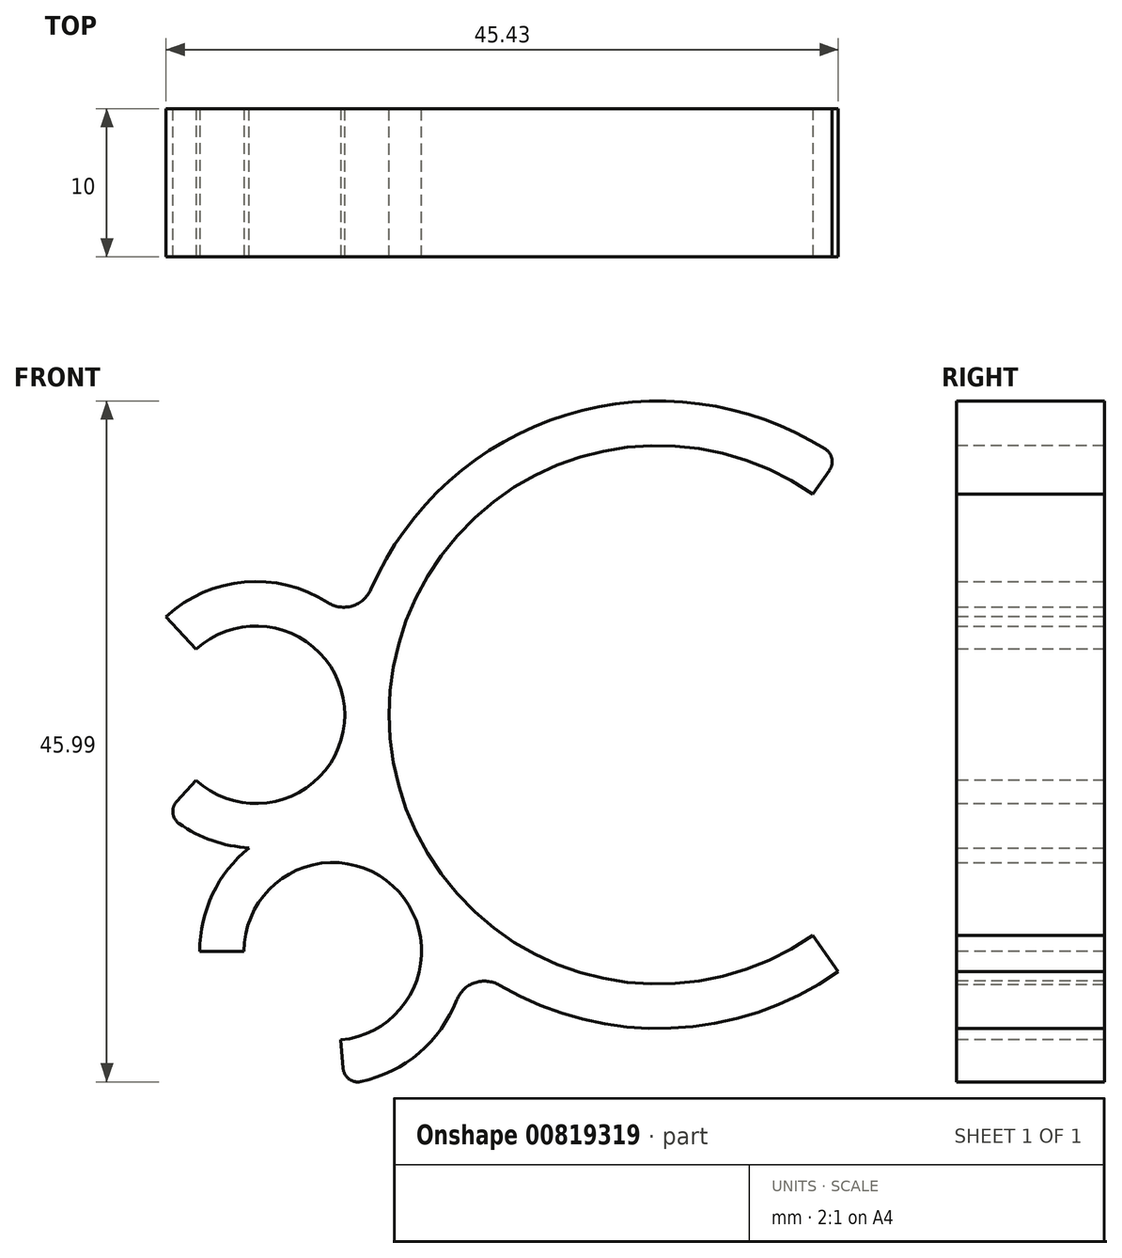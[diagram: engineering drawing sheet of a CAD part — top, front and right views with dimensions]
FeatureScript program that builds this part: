
annotation { "Feature Type Name" : "Feature", "Feature Type Description" : "" }
export const myFeature = defineFeature(function(context is Context, id is Id, definition is map)
    precondition{}
    {
        {
            var Q0;
            Q0=qCreatedBy(makeId("Front.planeOp"),FACE);
            var sketch = newSketch(context, id + "F0", { "sketchPlane" : qUnion([Q0])});
            skCircle(sketch, "E0", {"center": v(0, 0) * mm, "radius": 18.2 * mm});
            skCircle(sketch, "E1", {"center": v(0, 0) * mm, "radius": 21.2 * mm});
            skCircle(sketch, "E2", {"center": v(-27.2, 0) * mm, "radius": 6 * mm});
            skCircle(sketch, "E3", {"center": v(-27.2, 0) * mm, "radius": 9 * mm});
            skSolve(sketch);
        }
        {
            var Q0;
            Q0 = qSketchRegion(id + "F0", true);
            extrude(context, id + "F1", {"entities" : qUnion([Q0]), "endBound" : BoundingType.SYMMETRIC, "depth" : 10 * mm, "offsetDistance" : 25 * mm});
        }
        {
            var Q0;
            {var subQ0=sQuery(id+"F0.wireOp",EDGE,"E3");var subQ1=sQuery(id+"F0.wireOp",EDGE,"E1");Q0=makeQuery(id+"F1.opExtrude","SWEPT_EDGE",EDGE,{"disambiguationData":[OSD([subQ1,subQ0]),TDD([makeQuery(id+"F0.imprint","INTERSECT",VERTEX,{"disambiguationData":[OD(0.0)],"derivedFrom":[subQ1,subQ0]})])]});}
            var Q1;
            {var subQ0=sQuery(id+"F0.wireOp",EDGE,"E3");var subQ1=sQuery(id+"F0.wireOp",EDGE,"E1");Q1=makeQuery(id+"F1.opExtrude","SWEPT_EDGE",EDGE,{"disambiguationData":[OSD([subQ1,subQ0]),TDD([makeQuery(id+"F0.imprint","INTERSECT",VERTEX,{"disambiguationData":[OD(1.0)],"derivedFrom":[subQ1,subQ0]})])]});}
            fillet(context, id + "F2", {"entities" : qUnion([Q0, Q1]), "radius" : 2 * mm, "tangentPropagation" : true, "allowEdgeOverflow" : false});
        }
        {
            var Q0;
            Q0=makeQuery(id+"F1.opExtrude","SWEPT_BODY",BODY,{"disambiguationData":[OSD([sQuery(id+"F0.wireOp",EDGE,"E0"),sQuery(id+"F0.wireOp",EDGE,"E1"),sQuery(id+"F0.wireOp",EDGE,"E2"),sQuery(id+"F0.wireOp",EDGE,"E3")])]});
            var Q1;
            Q1=makeQuery(id+"F1.opExtrude","SWEPT_FACE",FACE,{"disambiguationData":[OSD([sQuery(id+"F0.wireOp",EDGE,"E0")])]});
            circularPattern(context, id + "F3", {"operationType" : NewBodyOperationType.ADD, "entities" : qUnion([Q0]), "axis" : qUnion([Q1]), "angle" : 36 * degree, "instanceCount" : 2, "equalSpace" : true});
        }
        {
            var Q0;
            Q0=makeQuery(id+"F1.opExtrude","CAP_FACE",FACE,{"disambiguationData":[OSD([sQuery(id+"F0.wireOp",EDGE,"E0"),sQuery(id+"F0.wireOp",EDGE,"E1"),sQuery(id+"F0.wireOp",EDGE,"E2"),sQuery(id+"F0.wireOp",EDGE,"E3")])],"isStart":false});
            var sketch = newSketch(context, id + "F4", { "sketchPlane" : qUnion([Q0])});
            skLineSegment(sketch, "E4", {"start": v(-31.25, 4.42) * mm, "end": v(-33.27, 6.64) * mm});
            skLineSegment(sketch, "E5", {"start": v(-31.25, -4.42) * mm, "end": v(-33.27, -6.64) * mm});
            skLineSegment(sketch, "E6", {"start": v(10.44, 14.9) * mm, "end": v(12.16, 17.36) * mm});
            skLineSegment(sketch, "E7", {"start": v(10.44, -14.9) * mm, "end": v(12.16, -17.36) * mm});
            skCircle(sketch, "E8.0", {"center": v(-27.2, 0) * mm, "radius": 6 * mm});
            skArc(sketch, "E9", {"start": v(-33.27, 6.64) * mm, "mid": v(-36.2, 0) * mm, "end": v(-33.27, -6.64) * mm});
            skArc(sketch, "E10", {"start": v(-31.25, 4.42) * mm, "mid": v(-33.2, 0) * mm, "end": v(-31.25, -4.42) * mm});
            skArc(sketch, "E11", {"start": v(10.44, 14.9) * mm, "mid": v(18.2, 0) * mm, "end": v(10.44, -14.9) * mm});
            skArc(sketch, "E12", {"start": v(12.16, 17.36) * mm, "mid": v(21.2, 0) * mm, "end": v(12.16, -17.36) * mm});
            skLineSegment(sketch, "E13", {"start": v(-28, -15.98) * mm, "end": v(-31, -15.98) * mm});
            skLineSegment(sketch, "E14", {"start": v(-21.48, -21.96) * mm, "end": v(-21.22, -24.95) * mm});
            skCircle(sketch, "E15.0", {"center": v(-22, -15.98) * mm, "radius": 6 * mm});
            skArc(sketch, "E16", {"start": v(-31, -15.98) * mm, "mid": v(-28.08, -22.62) * mm, "end": v(-21.22, -24.95) * mm});
            skArc(sketch, "E17", {"start": v(-28, -15.98) * mm, "mid": v(-26.05, -20.4) * mm, "end": v(-21.48, -21.96) * mm});
            skSolve(sketch);
        }
        {
            var Q0;
            {var subQ0=sQuery(id+"F4.wireOp",EDGE,"E4");Q0=makeQuery(id+"F4.imprint","IMPRINT",FACE,{"disambiguationData":[TD([[makeQuery(id+"F4.imprint","IMPRINT",EDGE,{"derivedFrom":subQ0}),1.0]])]});}
            var Q1;
            Q1=makeQuery(id+"F4.imprint","IMPRINT",FACE,{"disambiguationData":[TD([[makeQuery(id+"F4.imprint","IMPRINT",EDGE,{"derivedFrom":sQuery(id+"F4.wireOp",EDGE,"E6")}),-1.0]])]});
            var Q2;
            {var subQ0=sQuery(id+"F4.wireOp",EDGE,"E13");Q2=makeQuery(id+"F4.imprint","IMPRINT",FACE,{"disambiguationData":[TD([[makeQuery(id+"F4.imprint","IMPRINT",EDGE,{"derivedFrom":subQ0}),1.0]])]});}
            extrude(context, id + "F5", {"entities" : qUnion([Q0, Q1, Q2]), "operationType" : NewBodyOperationType.REMOVE, "endBound" : BoundingType.THROUGH_ALL, "oppositeDirection" : true, "depth" : 25 * mm, "offsetDistance" : 25 * mm});
        }
        {
            var Q0;
            Q0=makeQuery(id+"F5.boolean.opBoolean","COPY",EDGE,{"derivedFrom":makeQuery(id+"F5.opExtrude","SWEPT_EDGE",EDGE,{"disambiguationData":[OSD([sQuery(id+"F4.wireOp",EDGE,"E4"),sQuery(id+"F4.wireOp",EDGE,"E8.0")])]})});
            var Q1;
            Q1=makeQuery(id+"F5.boolean.opBoolean","COPY",EDGE,{"derivedFrom":makeQuery(id+"F5.opExtrude","SWEPT_EDGE",EDGE,{"disambiguationData":[OSD([sQuery(id+"F0.wireOp",EDGE,"E3"),sQuery(id+"F4.wireOp",EDGE,"E4"),sQuery(id+"F4.wireOp",EDGE,"E9")])]})});
            var Q2;
            Q2=makeQuery(id+"F5.boolean.opBoolean","COPY",EDGE,{"derivedFrom":makeQuery(id+"F5.opExtrude","SWEPT_EDGE",EDGE,{"disambiguationData":[OSD([sQuery(id+"F0.wireOp",EDGE,"E3"),sQuery(id+"F4.wireOp",EDGE,"E5"),sQuery(id+"F4.wireOp",EDGE,"E9")])]})});
            var Q3;
            Q3=makeQuery(id+"F5.boolean.opBoolean","COPY",EDGE,{"derivedFrom":makeQuery(id+"F5.opExtrude","SWEPT_EDGE",EDGE,{"disambiguationData":[OSD([sQuery(id+"F4.wireOp",EDGE,"E5"),sQuery(id+"F4.wireOp",EDGE,"E8.0")])]})});
            var Q4;
            Q4=makeQuery(id+"F5.boolean.opBoolean","COPY",EDGE,{"derivedFrom":makeQuery(id+"F5.opExtrude","SWEPT_EDGE",EDGE,{"disambiguationData":[OSD([sQuery(id+"F0.wireOp",EDGE,"E0"),sQuery(id+"F4.wireOp",EDGE,"E6"),sQuery(id+"F4.wireOp",EDGE,"E11")])]})});
            var Q5;
            Q5=makeQuery(id+"F5.boolean.opBoolean","COPY",EDGE,{"derivedFrom":makeQuery(id+"F5.opExtrude","SWEPT_EDGE",EDGE,{"disambiguationData":[OSD([sQuery(id+"F0.wireOp",EDGE,"E1"),sQuery(id+"F4.wireOp",EDGE,"E6"),sQuery(id+"F4.wireOp",EDGE,"E12")])]})});
            var Q6;
            Q6=makeQuery(id+"F5.boolean.opBoolean","COPY",EDGE,{"derivedFrom":makeQuery(id+"F5.opExtrude","SWEPT_EDGE",EDGE,{"disambiguationData":[OSD([sQuery(id+"F0.wireOp",EDGE,"E1"),sQuery(id+"F4.wireOp",EDGE,"E7"),sQuery(id+"F4.wireOp",EDGE,"E12")])]})});
            var Q7;
            Q7=makeQuery(id+"F5.boolean.opBoolean","COPY",EDGE,{"derivedFrom":makeQuery(id+"F5.opExtrude","SWEPT_EDGE",EDGE,{"disambiguationData":[OSD([sQuery(id+"F0.wireOp",EDGE,"E0"),sQuery(id+"F4.wireOp",EDGE,"E7"),sQuery(id+"F4.wireOp",EDGE,"E11")])]})});
            var Q8;
            Q8=makeQuery(id+"F5.boolean.opBoolean","COPY",EDGE,{"derivedFrom":makeQuery(id+"F5.opExtrude","SWEPT_EDGE",EDGE,{"disambiguationData":[OSD([sQuery(id+"F4.wireOp",EDGE,"E13"),sQuery(id+"F4.wireOp",EDGE,"E15.0")])]})});
            var Q9;
            Q9=makeQuery(id+"F5.boolean.opBoolean","COPY",EDGE,{"derivedFrom":makeQuery(id+"F5.opExtrude","SWEPT_EDGE",EDGE,{"disambiguationData":[OSD([sQuery(id+"F0.wireOp",EDGE,"E3"),sQuery(id+"F4.wireOp",EDGE,"E13"),sQuery(id+"F4.wireOp",EDGE,"E16")])]})});
            var Q10;
            Q10=makeQuery(id+"F5.boolean.opBoolean","COPY",EDGE,{"derivedFrom":makeQuery(id+"F5.opExtrude","SWEPT_EDGE",EDGE,{"disambiguationData":[OSD([sQuery(id+"F4.wireOp",EDGE,"E14"),sQuery(id+"F4.wireOp",EDGE,"E15.0")])]})});
            var Q11;
            Q11=makeQuery(id+"F5.boolean.opBoolean","COPY",EDGE,{"derivedFrom":makeQuery(id+"F5.opExtrude","SWEPT_EDGE",EDGE,{"disambiguationData":[OSD([sQuery(id+"F0.wireOp",EDGE,"E3"),sQuery(id+"F4.wireOp",EDGE,"E14"),sQuery(id+"F4.wireOp",EDGE,"E16")])]})});
            fillet(context, id + "F6", {"entities" : qUnion([Q0, Q1, Q2, Q3, Q4, Q5, Q6, Q7, Q8, Q9, Q10, Q11]), "radius" : 1 * mm, "tangentPropagation" : true, "allowEdgeOverflow" : false});
        }
    });
